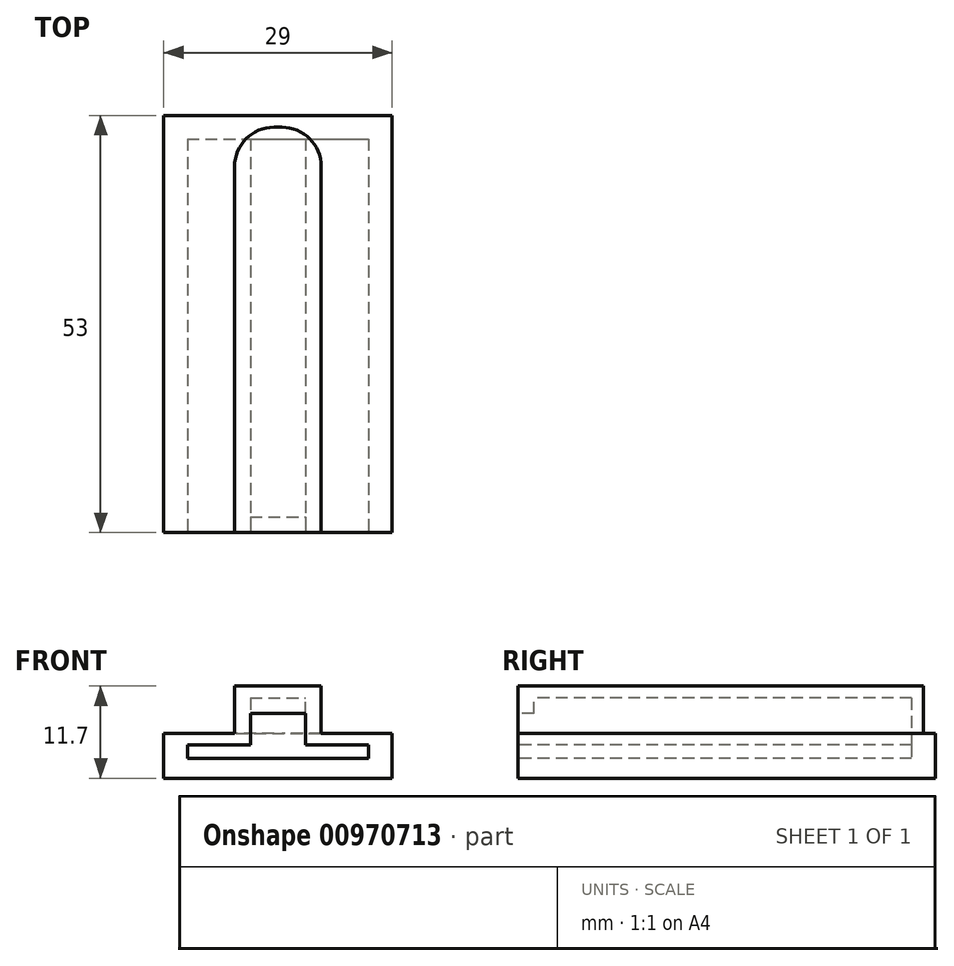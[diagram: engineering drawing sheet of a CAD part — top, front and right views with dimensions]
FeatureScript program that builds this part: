
annotation { "Feature Type Name" : "Feature", "Feature Type Description" : "" }
export const myFeature = defineFeature(function(context is Context, id is Id, definition is map)
    precondition{}
    {
        {
            var Q0;
            Q0=qCreatedBy(makeId("Top.planeOp"),FACE);
            var sketch = newSketch(context, id + "F0", { "sketchPlane" : qUnion([Q0])});
            skLineSegment(sketch, "E0.bottom", {"start": v(-26, 8.73) * mm, "end": v(-3, 8.73) * mm});
            skLineSegment(sketch, "E0.top", {"start": v(-26, -41.27) * mm, "end": v(-3, -41.27) * mm});
            skLineSegment(sketch, "E0.left", {"start": v(-26, 8.73) * mm, "end": v(-26, -41.27) * mm});
            skLineSegment(sketch, "E0.right", {"start": v(-3, 8.73) * mm, "end": v(-3, -41.27) * mm});
            skPoint(sketch, "E1", {"position": v(-26, 11.73) * mm});
            skPoint(sketch, "E2", {"position": v(-29, 11.73) * mm});
            skPoint(sketch, "E3", {"position": v(-3, -44.27) * mm});
            skPoint(sketch, "E4", {"position": v(0, -44.27) * mm});
            skLineSegment(sketch, "E5.bottom", {"start": v(-29, 11.73) * mm, "end": v(0, 11.73) * mm});
            skLineSegment(sketch, "E5.top", {"start": v(-29, -41.27) * mm, "end": v(0, -41.27) * mm});
            skLineSegment(sketch, "E5.left", {"start": v(-29, 11.73) * mm, "end": v(-29, -41.27) * mm});
            skLineSegment(sketch, "E5.right", {"start": v(0, 11.73) * mm, "end": v(0, -41.27) * mm});
            skSolve(sketch);
        }
        {
            var Q0;
            Q0=makeQuery(id+"F0.imprint","IMPRINT",FACE,{"disambiguationData":[TD([[makeQuery(id+"F0.imprint","IMPRINT",EDGE,{"derivedFrom":sQuery(id+"F0.wireOp",EDGE,"E0.bottom")}),-1.0]])]});
            extrude(context, id + "F1", {"entities" : qUnion([Q0]), "depth" : 1.5 * mm, "offsetDistance" : 25 * mm});
        }
        {
            var Q0;
            Q0=makeQuery(id+"F0.imprint","IMPRINT",FACE,{"disambiguationData":[TD([[makeQuery(id+"F0.imprint","IMPRINT",EDGE,{"derivedFrom":sQuery(id+"F0.wireOp",EDGE,"E0.bottom")}),1.0]])]});
            extrude(context, id + "F2", {"entities" : qUnion([Q0]), "operationType" : NewBodyOperationType.ADD, "depth" : 3.2 * mm, "offsetDistance" : 25 * mm});
        }
        {
            var Q0;
            Q0=makeQuery(id+"F2.opExtrude","CAP_FACE",FACE,{"disambiguationData":[OSD([sQuery(id+"F0.wireOp",EDGE,"E0.bottom"),sQuery(id+"F0.wireOp",EDGE,"E0.left"),sQuery(id+"F0.wireOp",EDGE,"E0.right"),sQuery(id+"F0.wireOp",EDGE,"E5.bottom"),sQuery(id+"F0.wireOp",EDGE,"E5.top"),sQuery(id+"F0.wireOp",EDGE,"E5.left"),sQuery(id+"F0.wireOp",EDGE,"E5.right")])],"isStart":false});
            var sketch = newSketch(context, id + "F3", { "sketchPlane" : qUnion([Q0])});
            skLineSegment(sketch, "E6.bottom", {"start": v(-29, 11.73) * mm, "end": v(-18, 11.73) * mm});
            skLineSegment(sketch, "E6.top", {"start": v(-29, -41.27) * mm, "end": v(-18, -41.27) * mm});
            skLineSegment(sketch, "E6.left", {"start": v(-29, 11.73) * mm, "end": v(-29, -41.27) * mm});
            skLineSegment(sketch, "E6.right", {"start": v(-18, 11.73) * mm, "end": v(-18, -41.27) * mm});
            skLineSegment(sketch, "E7.bottom", {"start": v(0, 11.73) * mm, "end": v(-11, 11.73) * mm});
            skLineSegment(sketch, "E7.top", {"start": v(0, -41.27) * mm, "end": v(-11, -41.27) * mm});
            skLineSegment(sketch, "E7.left", {"start": v(0, 11.73) * mm, "end": v(0, -41.27) * mm});
            skLineSegment(sketch, "E7.right", {"start": v(-11, 11.73) * mm, "end": v(-11, -41.27) * mm});
            skLineSegment(sketch, "E8.bottom", {"start": v(-18, 11.73) * mm, "end": v(-11, 11.73) * mm});
            skLineSegment(sketch, "E8.top", {"start": v(-18, 8.73) * mm, "end": v(-11, 8.73) * mm});
            skLineSegment(sketch, "E8.left", {"start": v(-18, 11.73) * mm, "end": v(-18, 8.73) * mm});
            skLineSegment(sketch, "E8.right", {"start": v(-11, 11.73) * mm, "end": v(-11, 8.73) * mm});
            skLineSegment(sketch, "E9.bottom", {"start": v(-18, 8.73) * mm, "end": v(-20, 8.73) * mm});
            skLineSegment(sketch, "E9.top", {"start": v(-18, -41.27) * mm, "end": v(-20, -41.27) * mm});
            skLineSegment(sketch, "E9.left", {"start": v(-18, 8.73) * mm, "end": v(-18, -41.27) * mm});
            skLineSegment(sketch, "E9.right", {"start": v(-20, 8.73) * mm, "end": v(-20, -41.27) * mm});
            skLineSegment(sketch, "E10.bottom", {"start": v(-11, 8.73) * mm, "end": v(-9, 8.73) * mm});
            skLineSegment(sketch, "E10.top", {"start": v(-11, -41.27) * mm, "end": v(-9, -41.27) * mm});
            skLineSegment(sketch, "E10.left", {"start": v(-11, 8.73) * mm, "end": v(-11, -41.27) * mm});
            skLineSegment(sketch, "E10.right", {"start": v(-9, 8.73) * mm, "end": v(-9, -41.27) * mm});
            skSolve(sketch);
        }
        {
            var Q0;
            {var subQ0=sQuery(id+"F3.wireOp",EDGE,"E8.bottom");Q0=makeQuery(id+"F3.imprint","IMPRINT",FACE,{"disambiguationData":[TD([[makeQuery(id+"F3.imprint","IMPRINT",EDGE,{"derivedFrom":subQ0}),-1.0]])]});}
            var Q1;
            {var subQ2=sQuery(id+"F3.wireOp",EDGE,"E9.right");Q1=makeQuery(id+"F3.imprint","IMPRINT",FACE,{"disambiguationData":[TD([[makeQuery(id+"F3.imprint","IMPRINT",EDGE,{"derivedFrom":subQ2}),-1.0]])]});}
            var Q2;
            {var subQ2=sQuery(id+"F3.wireOp",EDGE,"E10.right");Q2=makeQuery(id+"F3.imprint","IMPRINT",FACE,{"disambiguationData":[TD([[makeQuery(id+"F3.imprint","IMPRINT",EDGE,{"derivedFrom":subQ2}),1.0]])]});}
            var Q3;
            {var subQ2=sQuery(id+"F3.wireOp",EDGE,"E6.bottom");Q3=makeQuery(id+"F3.imprint","IMPRINT",FACE,{"disambiguationData":[TD([[makeQuery(id+"F3.imprint","IMPRINT",EDGE,{"derivedFrom":subQ2}),-1.0]])]});}
            var Q4;
            {var subQ2=sQuery(id+"F3.wireOp",EDGE,"E7.bottom");Q4=makeQuery(id+"F3.imprint","IMPRINT",FACE,{"disambiguationData":[TD([[makeQuery(id+"F3.imprint","IMPRINT",EDGE,{"derivedFrom":subQ2}),-1.0]])]});}
            extrude(context, id + "F4", {"entities" : qUnion([Q0, Q1, Q2, Q3, Q4]), "operationType" : NewBodyOperationType.ADD, "depth" : 1.5 * mm, "offsetDistance" : 25 * mm});
        }
        {
            var Q0;
            {var subQ4=sQuery(id+"F3.wireOp",EDGE,"E10.bottom");Q0=makeQuery(id+"F3.imprint","IMPRINT",FACE,{"disambiguationData":[TD([[makeQuery(id+"F3.imprint","IMPRINT",EDGE,{"derivedFrom":subQ4}),-1.0]])]});}
            var Q1;
            {var subQ4=sQuery(id+"F3.wireOp",EDGE,"E9.bottom");Q1=makeQuery(id+"F3.imprint","IMPRINT",FACE,{"disambiguationData":[TD([[makeQuery(id+"F3.imprint","IMPRINT",EDGE,{"derivedFrom":subQ4}),-1.0]])]});}
            extrude(context, id + "F5", {"entities" : qUnion([Q0, Q1]), "operationType" : NewBodyOperationType.ADD, "depth" : 6 * mm, "offsetDistance" : 25 * mm});
        }
        {
            var Q0;
            Q0=makeQuery(id+"F4.opExtrude","CAP_FACE",FACE,{"disambiguationData":[OSD([sQuery(id+"F3.wireOp",EDGE,"E6.bottom"),sQuery(id+"F3.wireOp",EDGE,"E6.top"),sQuery(id+"F3.wireOp",EDGE,"E6.left"),sQuery(id+"F3.wireOp",EDGE,"E7.bottom"),sQuery(id+"F3.wireOp",EDGE,"E7.top"),sQuery(id+"F3.wireOp",EDGE,"E7.left"),sQuery(id+"F3.wireOp",EDGE,"E8.bottom"),sQuery(id+"F3.wireOp",EDGE,"E8.top"),sQuery(id+"F3.wireOp",EDGE,"E9.bottom"),sQuery(id+"F3.wireOp",EDGE,"E9.right"),sQuery(id+"F3.wireOp",EDGE,"E10.bottom"),sQuery(id+"F3.wireOp",EDGE,"E10.right")])],"isStart":false});
            var sketch = newSketch(context, id + "F6", { "sketchPlane" : qUnion([Q0])});
            skLineSegment(sketch, "E11.bottom", {"start": v(-20, 8.73) * mm, "end": v(-9, 8.73) * mm});
            skLineSegment(sketch, "E11.top", {"start": v(-20, 10.23) * mm, "end": v(-9, 10.23) * mm});
            skLineSegment(sketch, "E11.left", {"start": v(-20, 8.73) * mm, "end": v(-20, 10.23) * mm});
            skLineSegment(sketch, "E11.right", {"start": v(-9, 8.73) * mm, "end": v(-9, 10.23) * mm});
            skSolve(sketch);
        }
        {
            var Q0;
            Q0 = qSketchRegion(id + "F6", true);
            extrude(context, id + "F7", {"entities" : qUnion([Q0]), "operationType" : NewBodyOperationType.ADD, "depth" : 4.5 * mm, "offsetDistance" : 25 * mm});
        }
        {
            var Q0;
            Q0=makeQuery(id+"F7.boolean.opBoolean","MERGE",FACE,{"derivedFrom":[makeQuery(id+"F5.opExtrude","CAP_FACE",FACE,{"disambiguationData":[OSD([sQuery(id+"F3.wireOp",EDGE,"E6.top"),sQuery(id+"F3.wireOp",EDGE,"E6.right"),sQuery(id+"F3.wireOp",EDGE,"E9.bottom"),sQuery(id+"F3.wireOp",EDGE,"E9.right")])],"isStart":false}),makeQuery(id+"F5.opExtrude","CAP_FACE",FACE,{"disambiguationData":[OSD([sQuery(id+"F3.wireOp",EDGE,"E7.top"),sQuery(id+"F3.wireOp",EDGE,"E7.right"),sQuery(id+"F3.wireOp",EDGE,"E10.bottom"),sQuery(id+"F3.wireOp",EDGE,"E10.right")])],"isStart":false}),makeQuery(id+"F7.opExtrude","CAP_FACE",FACE,{"disambiguationData":[OSD([sQuery(id+"F6.wireOp",EDGE,"E11.bottom"),sQuery(id+"F6.wireOp",EDGE,"E11.top"),sQuery(id+"F6.wireOp",EDGE,"E11.left"),sQuery(id+"F6.wireOp",EDGE,"E11.right")])],"isStart":false})]});
            var sketch = newSketch(context, id + "F8", { "sketchPlane" : qUnion([Q0])});
            skLineSegment(sketch, "E12.bottom", {"start": v(-20, 10.23) * mm, "end": v(-9, 10.23) * mm});
            skLineSegment(sketch, "E12.top", {"start": v(-20, -41.27) * mm, "end": v(-9, -41.27) * mm});
            skLineSegment(sketch, "E12.left", {"start": v(-20, 10.23) * mm, "end": v(-20, -41.27) * mm});
            skLineSegment(sketch, "E12.right", {"start": v(-9, 10.23) * mm, "end": v(-9, -41.27) * mm});
            skSolve(sketch);
        }
        {
            var Q0;
            Q0 = qSketchRegion(id + "F8", true);
            extrude(context, id + "F9", {"entities" : qUnion([Q0]), "operationType" : NewBodyOperationType.ADD, "depth" : 1.5 * mm, "offsetDistance" : 25 * mm});
        }
        {
            var Q0;
            Q0=makeQuery(id+"F9.boolean.opBoolean","MERGE",EDGE,{"derivedFrom":[makeQuery(id+"F7.opExtrude","SWEPT_EDGE",EDGE,{"disambiguationData":[OSD([sQuery(id+"F6.wireOp",EDGE,"E11.top"),sQuery(id+"F6.wireOp",EDGE,"E11.left")])]}),makeQuery(id+"F9.opExtrude","SWEPT_EDGE",EDGE,{"disambiguationData":[OSD([sQuery(id+"F8.wireOp",EDGE,"E12.bottom"),sQuery(id+"F8.wireOp",EDGE,"E12.left")])]})]});
            var Q1;
            Q1=makeQuery(id+"F9.boolean.opBoolean","MERGE",EDGE,{"derivedFrom":[makeQuery(id+"F7.opExtrude","SWEPT_EDGE",EDGE,{"disambiguationData":[OSD([sQuery(id+"F6.wireOp",EDGE,"E11.top"),sQuery(id+"F6.wireOp",EDGE,"E11.right")])]}),makeQuery(id+"F9.opExtrude","SWEPT_EDGE",EDGE,{"disambiguationData":[OSD([sQuery(id+"F8.wireOp",EDGE,"E12.bottom"),sQuery(id+"F8.wireOp",EDGE,"E12.right")])]})]});
            fillet(context, id + "F10", {"entities" : qUnion([Q0, Q1]), "radius" : 5 * mm, "tangentPropagation" : true, "allowEdgeOverflow" : false});
        }
        {
            var Q0;
            {var subQ0=sQuery(id+"F0.wireOp",EDGE,"E0.right");var subQ1=sQuery(id+"F0.wireOp",EDGE,"E0.left");var subQ2=sQuery(id+"F0.wireOp",EDGE,"E0.bottom");Q0=makeQuery(id+"F2.boolean.opBoolean","MERGE",FACE,{"derivedFrom":[makeQuery(id+"F1.opExtrude","CAP_FACE",FACE,{"disambiguationData":[OSD([subQ2,sQuery(id+"F0.wireOp",EDGE,"E0.top"),subQ1,subQ0])],"isStart":true}),makeQuery(id+"F2.opExtrude","CAP_FACE",FACE,{"disambiguationData":[OSD([subQ2,subQ1,subQ0,sQuery(id+"F0.wireOp",EDGE,"E5.bottom"),sQuery(id+"F0.wireOp",EDGE,"E5.top"),sQuery(id+"F0.wireOp",EDGE,"E5.left"),sQuery(id+"F0.wireOp",EDGE,"E5.right")])],"isStart":true})]});}
            var sketch = newSketch(context, id + "F11", { "sketchPlane" : qUnion([Q0])});
            skLineSegment(sketch, "E13.bottom", {"start": v(-29, 41.27) * mm, "end": v(0, 41.27) * mm});
            skLineSegment(sketch, "E13.top", {"start": v(-29, -11.73) * mm, "end": v(0, -11.73) * mm});
            skLineSegment(sketch, "E13.left", {"start": v(-29, 41.27) * mm, "end": v(-29, -11.73) * mm});
            skLineSegment(sketch, "E13.right", {"start": v(0, 41.27) * mm, "end": v(0, -11.73) * mm});
            skSolve(sketch);
        }
        {
            var Q0;
            Q0 = qSketchRegion(id + "F11", true);
            extrude(context, id + "F12", {"entities" : qUnion([Q0]), "operationType" : NewBodyOperationType.ADD, "depth" : 1 * mm, "offsetDistance" : 25 * mm});
        }
        {
            var Q0;
            Q0=makeQuery(id+"F9.opExtrude","CAP_FACE",FACE,{"disambiguationData":[OSD([sQuery(id+"F8.wireOp",EDGE,"E12.bottom"),sQuery(id+"F8.wireOp",EDGE,"E12.top"),sQuery(id+"F8.wireOp",EDGE,"E12.left"),sQuery(id+"F8.wireOp",EDGE,"E12.right")])],"isStart":true});
            var sketch = newSketch(context, id + "F13", { "sketchPlane" : qUnion([Q0])});
            skLineSegment(sketch, "E14.bottom", {"start": v(-18, 41.27) * mm, "end": v(-11, 41.27) * mm});
            skLineSegment(sketch, "E14.top", {"start": v(-18, 39.27) * mm, "end": v(-11, 39.27) * mm});
            skLineSegment(sketch, "E14.left", {"start": v(-18, 41.27) * mm, "end": v(-18, 39.27) * mm});
            skLineSegment(sketch, "E14.right", {"start": v(-11, 41.27) * mm, "end": v(-11, 39.27) * mm});
            skSolve(sketch);
        }
        {
            var Q0;
            Q0 = qSketchRegion(id + "F13", true);
            extrude(context, id + "F14", {"entities" : qUnion([Q0]), "operationType" : NewBodyOperationType.ADD, "depth" : 2 * mm, "offsetDistance" : 25 * mm});
        }
    });
